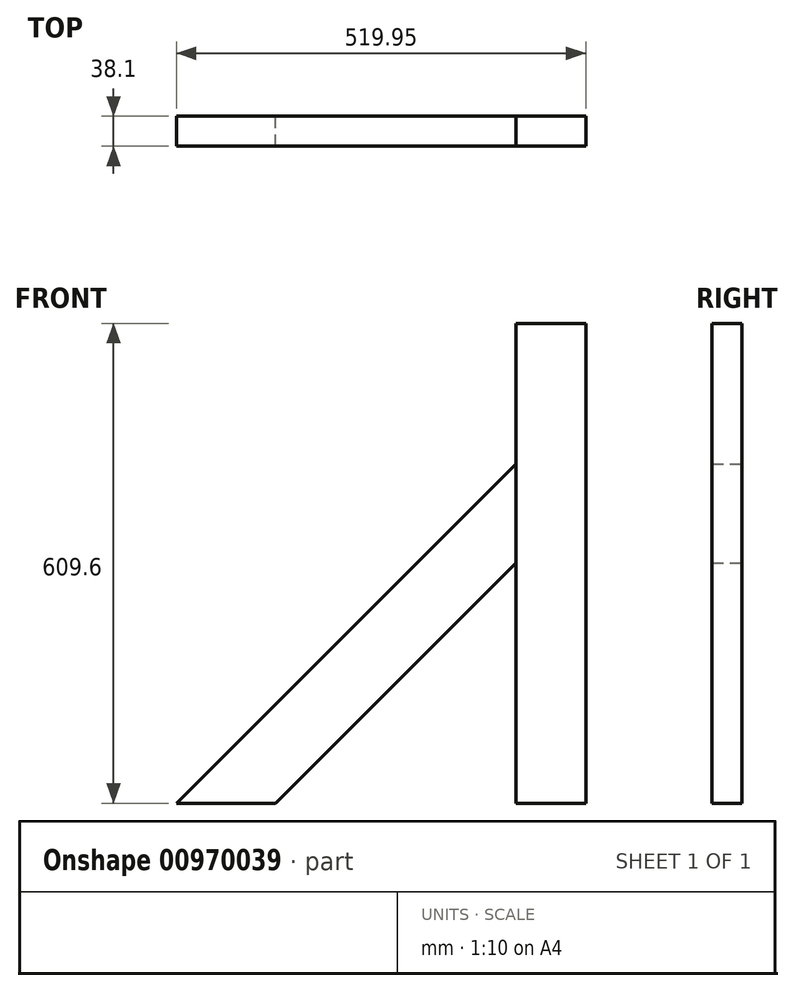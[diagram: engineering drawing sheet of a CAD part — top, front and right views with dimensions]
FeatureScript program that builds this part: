
annotation { "Feature Type Name" : "Feature", "Feature Type Description" : "" }
export const myFeature = defineFeature(function(context is Context, id is Id, definition is map)
    precondition{}
    {
        {
            var Q0;
            Q0=qCreatedBy(makeId("Front.planeOp"),FACE);
            var sketch = newSketch(context, id + "F0", { "sketchPlane" : qUnion([Q0])});
            skLineSegment(sketch, "E0.bottom", {"start": v(0, 0) * mm, "end": v(88.9, 0) * mm});
            skLineSegment(sketch, "E0.top", {"start": v(0, 609.6) * mm, "end": v(88.9, 609.6) * mm});
            skLineSegment(sketch, "E0.left", {"start": v(0, 0) * mm, "end": v(0, 609.6) * mm});
            skLineSegment(sketch, "E0.right", {"start": v(88.9, 0) * mm, "end": v(88.9, 609.6) * mm});
            skSolve(sketch);
        }
        {
            var Q0;
            Q0=makeQuery(id+"F0.imprint","IMPRINT",FACE,{"disambiguationData":[TD([[makeQuery(id+"F0.imprint","IMPRINT",EDGE,{"derivedFrom":sQuery(id+"F0.wireOp",EDGE,"E0.bottom")}),1.0]])]});
            extrude(context, id + "F1", {"entities" : qUnion([Q0]), "endBound" : BoundingType.SYMMETRIC, "depth" : 38.1 * mm, "offsetDistance" : 25.4 * mm});
        }
        {
            var Q0;
            Q0=qCreatedBy(makeId("Front.planeOp"),FACE);
            var sketch = newSketch(context, id + "F2", { "sketchPlane" : qUnion([Q0])});
            skLineSegment(sketch, "E1", {"start": v(0, 431.05) * mm, "end": v(-431.05, 0) * mm});
            skLineSegment(sketch, "E2", {"start": v(-431.05, 0) * mm, "end": v(-305.33, 0) * mm});
            skLineSegment(sketch, "E3", {"start": v(-305.33, 0) * mm, "end": v(0, 305.33) * mm});
            skLineSegment(sketch, "E4", {"start": v(0, 305.33) * mm, "end": v(0, 431.05) * mm});
            skSolve(sketch);
        }
        {
            var Q0;
            Q0=makeQuery(id+"F2.imprint","IMPRINT",FACE,{"disambiguationData":[TD([[makeQuery(id+"F2.imprint","IMPRINT",EDGE,{"derivedFrom":sQuery(id+"F2.wireOp",EDGE,"E1")}),1.0]])]});
            extrude(context, id + "F3", {"entities" : qUnion([Q0]), "endBound" : BoundingType.SYMMETRIC, "depth" : 38.1 * mm, "offsetDistance" : 25.4 * mm});
        }
    });
